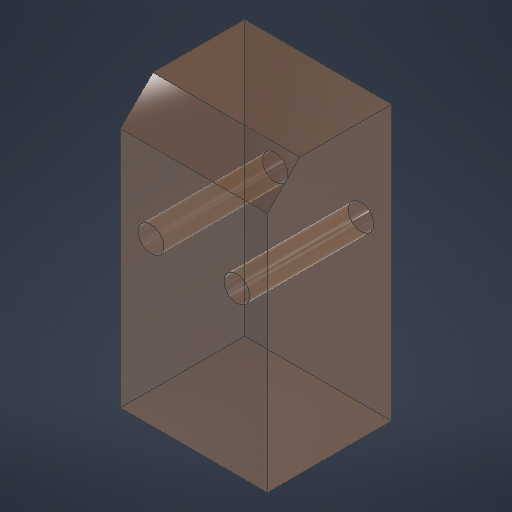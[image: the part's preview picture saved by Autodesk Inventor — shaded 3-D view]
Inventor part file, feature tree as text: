
AUTODESK INVENTOR PART (.ipt)
format: ipt  version: 2025 (Build 290162000, 162)  size: 217,088 bytes
history: native  units: mm
features: extrude x1, chamfer x1, sketch x1, other x1
ambient origin geometry x8: Origin, YZ Plane, XZ Plane, XY Plane, X Axis, Y Axis, Z Axis, Center Point
bodies: Solid1 (feature_tree)
feature tree (4):
  extrude  "Extrusion1"  Depth=33.79mm
  chamfer  "Chamfer1"  Distance=13.9mm
  sketch  "Sketch1"  dims[d0=18.1mm d1=33.79mm d2=13.9mm d3=5.29mm d4=10.58mm d5=3.15mm d6=3.15mm d7=15.3mm d8=0.0mm d9=4.0mm d10=2.0mm d11=45.0deg]
  other  "Finish1"
